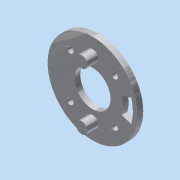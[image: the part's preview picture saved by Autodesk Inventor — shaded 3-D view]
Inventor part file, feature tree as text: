
AUTODESK INVENTOR PART (.ipt)
format: ipt  version: 2015 (Build 190159000, 159)  size: 160,256 bytes
history: native  units: in
note: dims shown in document units (in); Inventor stores cm internally (conversion verified against a paired STEP export)
features: other x4, extrude x2, sketch x1
ambient origin geometry x8: Origin, YZ Plane, XZ Plane, XY Plane, X Axis, Y Axis, Z Axis, Center Point
bodies: Solid1 (feature_tree)
feature tree (7):
  other  "StatorCore.ipt"
  sketch  "Sketch2"  dims[d0=0.3937in d1=0.25in d2=0.25in d3=0.625in d4=0.625in d5=0.125in d6=0.0in d7=0.3625in d8=0.0in]
  extrude  "Extrusion1"  Depth=0.25in
  extrude  "Extrusion2"  Depth=0.25in
  other  "TaggingFeature1"
  other  "Solid1::StatorCore.ipt"
  other  "Srf1"
